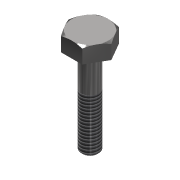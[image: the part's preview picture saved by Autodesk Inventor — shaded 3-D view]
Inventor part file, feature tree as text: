
AUTODESK INVENTOR PART (.ipt)
format: ipt  version: 2021 (Build 250183000, 183)  size: 192,512 bytes
history: native  units: in
note: dims shown in document units (in); Inventor stores cm internally (conversion verified against a paired STEP export)
features: other x121, thread x7, sketch x3, extrude x2, revolve x1, chamfer x1
ambient origin geometry x8: Origin, YZ Plane, XZ Plane, XY Plane, X Axis, Y Axis, Z Axis, Center Point
bodies: Solid1 (feature_tree)
feature tree (135):
  other  "Table"
  other  "BOLT-HH-A193-SS-0.500-1.25"
  other  "BOLT-HH-A193-SS-0.500-1.50"
  other  "BOLT-HH-A193-SS-0.500-1.75"
  other  "BOLT-HH-A193-SS-0.500-2.00"
  other  "BOLT-HH-A193-SS-0.500-2.25"
  other  "BOLT-HH-A193-SS-0.500-2.50"
  other  "BOLT-HH-A193-SS-0.500-2.75"
  other  "BOLT-HH-A193-SS-0.500-3.00"
  other  "BOLT-HH-A193-SS-0.500-3.50"
  other  "BOLT-HH-A193-SS-0.500-4.00"
  other  "BOLT-HH-A193-SS-0.625-1.25"
  other  "BOLT-HH-A193-SS-0.625-1.50"
  other  "BOLT-HH-A193-SS-0.625-1.75"
  other  "BOLT-HH-A193-SS-0.625-2.00"
  other  "BOLT-HH-A193-SS-0.625-2.25"
  other  "BOLT-HH-A193-SS-0.625-2.50"
  other  "BOLT-HH-A193-SS-0.625-2.75"
  other  "BOLT-HH-A193-SS-0.625-3.00"
  other  "BOLT-HH-A193-SS-0.625-3.25"
  other  "BOLT-HH-A193-SS-0.625-3.50"
  other  "BOLT-HH-A193-SS-0.625-3.75"
  other  "BOLT-HH-A193-SS-0.625-4.00"
  other  "BOLT-HH-A193-SS-0.625-4.25"
  other  "BOLT-HH-A193-SS-0.625-4.50"
  other  "BOLT-HH-A193-SS-0.625-4.75"
  other  "BOLT-HH-A193-SS-0.625-5.00"
  other  "BOLT-HH-A193-SS-0.625-5.50"
  other  "BOLT-HH-A193-SS-0.625-6.00"
  other  "BOLT-HH-A193-SS-0.75-1.50"
  other  "BOLT-HH-A193-SS-0.75-1.75"
  other  "BOLT-HH-A193-SS-0.75-2.00"
  other  "BOLT-HH-A193-SS-0.75-2.25"
  other  "BOLT-HH-A193-SS-0.75-2.50"
  other  "BOLT-HH-A193-SS-0.75-2.75"
  other  "BOLT-HH-A193-SS-0.75-3.00"
  other  "BOLT-HH-A193-SS-0.75-3.25"
  other  "BOLT-HH-A193-SS-0.75-3.50"
  other  "BOLT-HH-A193-SS-0.75-3.75"
  other  "BOLT-HH-A193-SS-0.75-4.00"
  other  "BOLT-HH-A193-SS-0.75-4.25"
  other  "BOLT-HH-A193-SS-0.75-4.50"
  other  "BOLT-HH-A193-SS-0.75-4.75"
  other  "BOLT-HH-A193-SS-0.75-5.00"
  other  "BOLT-HH-A193-SS-0.75-5.50"
  other  "BOLT-HH-A193-SS-0.75-6.00"
  other  "BOLT-HH-A193-SS-0.75-6.50"
  other  "BOLT-HH-A193-SS-0.75-7.00"
  other  "BOLT-HH-A193-SS-0.75-7.50"
  other  "BOLT-HH-A193-SS-0.75-8.00"
  other  "BOLT-HH-A193-SS-0.875-1.75"
  other  "BOLT-HH-A193-SS-0.875-2.00"
  other  "BOLT-HH-A193-SS-0.875-2.25"
  other  "BOLT-HH-A193-SS-0.875-2.50"
  other  "BOLT-HH-A193-SS-0.875-2.75"
  other  "BOLT-HH-A193-SS-0.875-3.00"
  other  "BOLT-HH-A193-SS-0.875-3.25"
  other  "BOLT-HH-A193-SS-0.875-3.50"
  other  "BOLT-HH-A193-SS-0.875-3.75"
  other  "BOLT-HH-A193-SS-0.875-4.00"
  other  "BOLT-HH-A193-SS-0.875-4.25"
  other  "BOLT-HH-A193-SS-0.875-4.50"
  other  "BOLT-HH-A193-SS-0.875-4.75"
  other  "BOLT-HH-A193-SS-0.875-5.00"
  other  "BOLT-HH-A193-SS-0.875-5.50"
  other  "BOLT-HH-A193-SS-0.875-6.00"
  other  "BOLT-HH-A193-SS-0.875-6.50"
  other  "BOLT-HH-A193-SS-0.875-7.00"
  other  "BOLT-HH-A193-SS-0.875-7.50"
  other  "BOLT-HH-A193-SS-0.875-8.00"
  other  "BOLT-HH-A193-SS-1.000-2.00"
  other  "BOLT-HH-A193-SS-1.000-2.25"
  other  "BOLT-HH-A193-SS-1.000-2.50"
  other  "BOLT-HH-A193-SS-1.000-2.75"
  other  "BOLT-HH-A193-SS-1.000-3.00"
  other  "BOLT-HH-A193-SS-1.000-3.25"
  other  "BOLT-HH-A193-SS-1.000-3.50"
  other  "BOLT-HH-A193-SS-1.000-3.75"
  other  "BOLT-HH-A193-SS-1.000-4.00"
  other  "BOLT-HH-A193-SS-1.000-4.25"
  other  "BOLT-HH-A193-SS-1.000-4.50"
  other  "BOLT-HH-A193-SS-1.000-4.75"
  other  "BOLT-HH-A193-SS-1.000-5.00"
  other  "BOLT-HH-A193-SS-1.000-5.50"
  other  "BOLT-HH-A193-SS-1.000-6.00"
  other  "BOLT-HH-A193-SS-1.000-6.50"
  other  "BOLT-HH-A193-SS-1.000-7.00"
  other  "BOLT-HH-A193-SS-1.000-7.50"
  other  "BOLT-HH-A193-SS-1.000-8.00"
  other  "BOLT-HH-A193-SS-1.125-2.75"
  other  "BOLT-HH-A193-SS-1.125-3.00"
  other  "BOLT-HH-A193-SS-1.125-3.25"
  other  "BOLT-HH-A193-SS-1.125-3.50"
  other  "BOLT-HH-A193-SS-1.125-3.75"
  other  "BOLT-HH-A193-SS-1.125-4.00"
  other  "BOLT-HH-A193-SS-1.125-4.25"
  other  "BOLT-HH-A193-SS-1.125-4.50"
  other  "BOLT-HH-A193-SS-1.125-4.75"
  other  "BOLT-HH-A193-SS-1.125-5.00"
  other  "BOLT-HH-A193-SS-1.125-5.50"
  other  "BOLT-HH-A193-SS-1.125-6.00"
  other  "BOLT-HH-A193-SS-1.125-6.50"
  other  "BOLT-HH-A193-SS-1.125-7.00"
  other  "BOLT-HH-A193-SS-1.125-7.50"
  other  "BOLT-HH-A193-SS-1.125-8.00"
  other  "BOLT-HH-A193-SS-1.250-3.00"
  other  "BOLT-HH-A193-SS-1.250-3.25"
  other  "BOLT-HH-A193-SS-1.250-3.50"
  other  "BOLT-HH-A193-SS-1.250-3.75"
  other  "BOLT-HH-A193-SS-1.250-4.00"
  other  "BOLT-HH-A193-SS-1.250-4.25"
  other  "BOLT-HH-A193-SS-1.250-4.50"
  other  "BOLT-HH-A193-SS-1.250-4.75"
  other  "BOLT-HH-A193-SS-1.250-5.00"
  other  "BOLT-HH-A193-SS-1.250-5.50"
  other  "BOLT-HH-A193-SS-1.250-6.00"
  other  "BOLT-HH-A193-SS-1.250-6.50"
  other  "BOLT-HH-A193-SS-1.250-7.00"
  other  "BOLT-HH-A193-SS-1.250-7.50"
  other  "BOLT-HH-A193-SS-1.250-8.00"
  other  "BOLT-HH-A193-SS-1.250-9.00"
  extrude  "Extrusion1"  TaperAngle=30.0deg  [1 undecoded]
  revolve  "Revolution1"  [1 undecoded]
  extrude  "Extrusion2"  TaperAngle=0.0deg  [1 undecoded]
  chamfer  "Chamfer1"  Distance=0.125in Angle=45.0deg
  thread  "Thread 1/2""  [1 undecoded]
  thread  "Thread 5/8""  [1 undecoded]
  thread  "Thread-3/4""  [1 undecoded]
  thread  "Thread 7/8""  [1 undecoded]
  thread  "Thread 1""  [1 undecoded]
  thread  "Thread 1 1/8""  [1 undecoded]
  thread  "Thread 1 1/4""  [1 undecoded]
  sketch  "Sketch1"  dims[d2=0.0in d3=30.0deg]
  sketch  "Sketch2"  dims[d5=0.5in d6=0.5in]
  sketch  "Sketch3"  dims[d7=90.0deg d10=0.0in d12=0.125in d13=45.0deg d15=0.0in d19=0.0in d21=0.0in d23=0.0in d25=0.0in d27=0.0in d29=0.0in d31=0.0in]
note: 10 required parameter values undecoded (feature->parameter linkage not recoverable at this tier; creation-order binding heuristic only, values carry confidence <= 0.55)